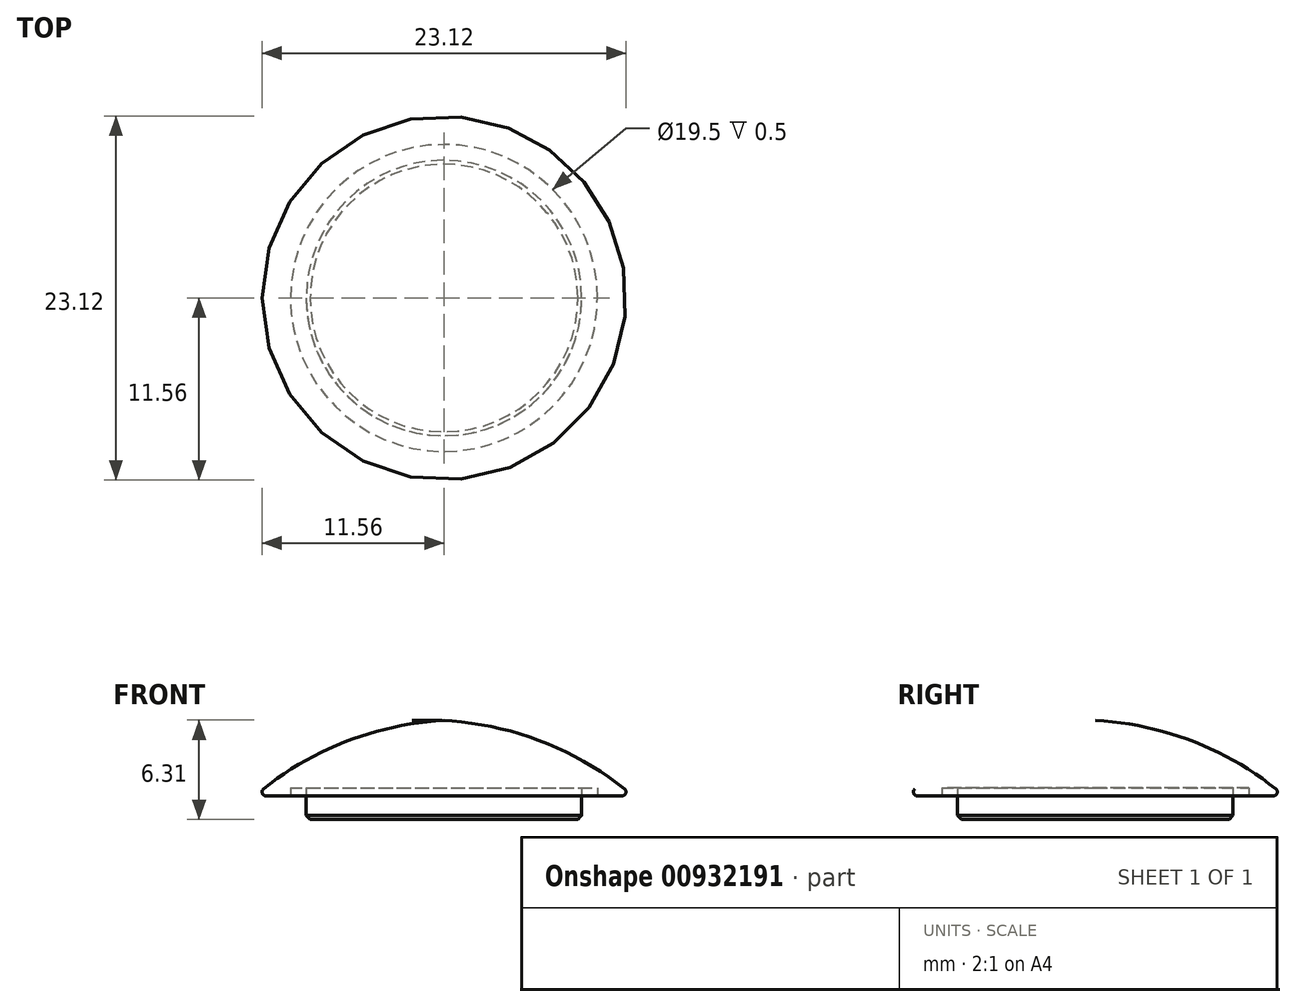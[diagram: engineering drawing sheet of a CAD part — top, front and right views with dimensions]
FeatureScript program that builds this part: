
annotation { "Feature Type Name" : "Feature", "Feature Type Description" : "" }
export const myFeature = defineFeature(function(context is Context, id is Id, definition is map)
    precondition{}
    {
        {
            var Q0;
            Q0=qCreatedBy(makeId("Front.planeOp"),FACE);
            var sketch = newSketch(context, id + "F0", { "sketchPlane" : qUnion([Q0])});
            skLineSegment(sketch, "E0", {"start": v(8.75, 0.22) * mm, "end": v(8.75, 0.72) * mm});
            skLineSegment(sketch, "E1", {"start": v(8.75, 0.72) * mm, "end": v(9.75, 0.72) * mm});
            skLineSegment(sketch, "E2", {"start": v(9.75, 0.72) * mm, "end": v(9.75, 0.22) * mm});
            skLineSegment(sketch, "E3", {"start": v(9.75, 0.22) * mm, "end": v(12, 0.22) * mm});
            skArc(sketch, "E4", {"start": v(12, 0.22) * mm, "mid": v(6.4, 3.6) * mm, "end": v(0, 5) * mm});
            skLineSegment(sketch, "E5", {"start": v(8.75, 0.22) * mm, "end": v(8.75, -1.28) * mm});
            skLineSegment(sketch, "E6", {"start": v(8.75, -1.28) * mm, "end": v(0, -1.28) * mm});
            skLineSegment(sketch, "E7", {"start": v(0, -1.28) * mm, "end": v(0, 5) * mm});
            skPoint(sketch, "E8.start.orphan", {"position": v(0, 0) * mm});
            skSolve(sketch);
        }
        {
            var Q0;
            Q0=makeQuery(id+"F0.imprint","IMPRINT",FACE,{"disambiguationData":[TD([[makeQuery(id+"F0.imprint","IMPRINT",EDGE,{"derivedFrom":sQuery(id+"F0.wireOp",EDGE,"E0")}),1.0]])]});
            var Q1;
            Q1=sQuery(id+"F0.wireOp",EDGE,"E7");
            revolve(context, id + "F1", {"surfaceOperationType" : NewSurfaceOperationType.NEW, "entities" : qUnion([Q0]), "axis" : qUnion([Q1]), "revolveType" : RevolveType.FULL});
        }
        {
            var Q0;
            Q0=makeQuery(id+"F1.opRevolve","SWEPT_EDGE",EDGE,{"disambiguationData":[OSD([sQuery(id+"F0.wireOp",EDGE,"E3"),sQuery(id+"F0.wireOp",EDGE,"E4")])]});
            fillet(context, id + "F2", {"entities" : qUnion([Q0]), "radius" : .25 * mm, "tangentPropagation" : true, "allowEdgeOverflow" : false});
        }
        {
            var Q0;
            Q0=makeQuery(id+"F1.opRevolve","SWEPT_EDGE",EDGE,{"disambiguationData":[OSD([sQuery(id+"F0.wireOp",EDGE,"E5"),sQuery(id+"F0.wireOp",EDGE,"E6")])]});
            chamfer(context, id + "F3", {"entities" : qUnion([Q0]), "width" : .25 * mm, "tangentPropagation" : true});
        }
    });
